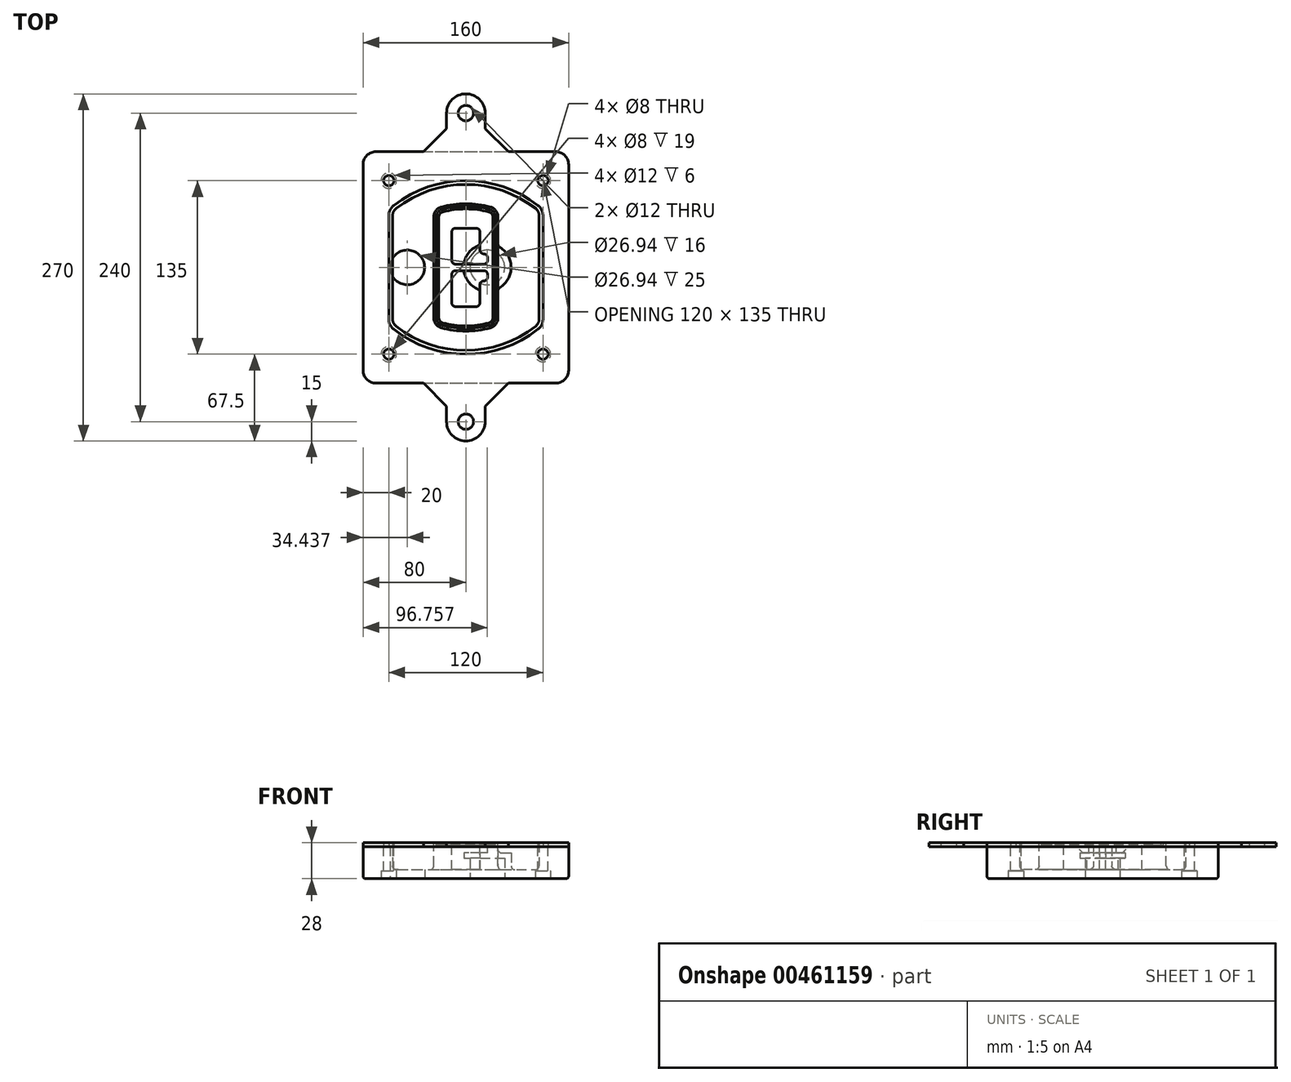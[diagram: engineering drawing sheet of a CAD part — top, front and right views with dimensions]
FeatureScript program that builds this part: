
annotation { "Feature Type Name" : "Feature", "Feature Type Description" : "" }
export const myFeature = defineFeature(function(context is Context, id is Id, definition is map)
    precondition{}
    {
        {
            var Q0;
            Q0=qCreatedBy(makeId("Top.planeOp"),FACE);
            var sketch = newSketch(context, id + "F0", { "sketchPlane" : qUnion([Q0])});
            skPoint(sketch, "E0.rect.middle", {"position": v(0, 0) * mm});
            skLineSegment(sketch, "E1.bottom", {"start": v(-70, -90) * mm, "end": v(70, -90) * mm});
            skLineSegment(sketch, "E1.top", {"start": v(-70, 90) * mm, "end": v(70, 90) * mm});
            skLineSegment(sketch, "E1.left", {"start": v(-80, -80) * mm, "end": v(-80, 80) * mm});
            skLineSegment(sketch, "E1.right", {"start": v(80, -80) * mm, "end": v(80, 80) * mm});
            skLineSegment(sketch, "E2", {"start": v(-80, 90) * mm, "end": v(80, -90) * mm, "construction": true});
            skLineSegment(sketch, "E3", {"start": v(80, 90) * mm, "end": v(-80, -90) * mm, "construction": true});
            skCircle(sketch, "E4", {"center": v(-60, 67.5) * mm, "radius": 4 * mm});
            skCircle(sketch, "E5", {"center": v(60, 67.5) * mm, "radius": 4 * mm});
            skCircle(sketch, "E6", {"center": v(60, -67.5) * mm, "radius": 4 * mm});
            skCircle(sketch, "E7", {"center": v(-60, -67.5) * mm, "radius": 4 * mm});
            skLineSegment(sketch, "E8", {"start": v(-60, 67.5) * mm, "end": v(60, 67.5) * mm, "construction": true});
            skLineSegment(sketch, "E9", {"start": v(60, 67.5) * mm, "end": v(60, -67.5) * mm, "construction": true});
            skLineSegment(sketch, "E10", {"start": v(60, -67.5) * mm, "end": v(-60, -67.5) * mm, "construction": true});
            skLineSegment(sketch, "E11", {"start": v(-60, -67.5) * mm, "end": v(-60, 67.5) * mm, "construction": true});
            skLineSegment(sketch, "E12", {"start": v(-60, 40.3) * mm, "end": v(-60, -40.3) * mm});
            skLineSegment(sketch, "E13", {"start": v(60, 40.3) * mm, "end": v(60, -40.3) * mm});
            skArc(sketch, "E14", {"start": v(56.15, 48.18) * mm, "mid": v(0, 67.5) * mm, "end": v(-56.15, 48.18) * mm});
            skArc(sketch, "E15", {"start": v(-56.15, -48.18) * mm, "mid": v(0, -67.5) * mm, "end": v(56.15, -48.18) * mm});
            skLineSegment(sketch, "E16", {"start": v(-60, 0) * mm, "end": v(60, 0) * mm, "construction": true});
            skPoint(sketch, "E17.visualSharp", {"position": v(-60, -45) * mm});
            skArc(sketch, "E17.filletArc", {"start": v(-60, -40.3) * mm, "mid": v(-58.99, -44.68) * mm, "end": v(-56.15, -48.18) * mm});
            skPoint(sketch, "E18.visualSharp", {"position": v(-60, 45) * mm});
            skArc(sketch, "E18.filletArc", {"start": v(-56.15, 48.18) * mm, "mid": v(-58.99, 44.68) * mm, "end": v(-60, 40.3) * mm});
            skPoint(sketch, "E19.visualSharp", {"position": v(60, 45) * mm});
            skArc(sketch, "E19.filletArc", {"start": v(60, 40.3) * mm, "mid": v(58.99, 44.68) * mm, "end": v(56.15, 48.18) * mm});
            skPoint(sketch, "E20.visualSharp", {"position": v(60, -45) * mm});
            skArc(sketch, "E20.filletArc", {"start": v(56.15, -48.18) * mm, "mid": v(58.99, -44.68) * mm, "end": v(60, -40.3) * mm});
            skPoint(sketch, "E21.visualSharp", {"position": v(-80, 90) * mm});
            skArc(sketch, "E21.filletArc", {"start": v(-70, 90) * mm, "mid": v(-77.07, 87.07) * mm, "end": v(-80, 80) * mm});
            skPoint(sketch, "E22.visualSharp", {"position": v(80, 90) * mm});
            skArc(sketch, "E22.filletArc", {"start": v(80, 80) * mm, "mid": v(77.07, 87.07) * mm, "end": v(70, 90) * mm});
            skPoint(sketch, "E23.visualSharp", {"position": v(80, -90) * mm});
            skArc(sketch, "E23.filletArc", {"start": v(70, -90) * mm, "mid": v(77.07, -87.07) * mm, "end": v(80, -80) * mm});
            skPoint(sketch, "E24.visualSharp", {"position": v(-80, -90) * mm});
            skArc(sketch, "E24.filletArc", {"start": v(-80, -80) * mm, "mid": v(-77.07, -87.07) * mm, "end": v(-70, -90) * mm});
            skArc(sketch, "E25.0", {"start": v(57, 40.3) * mm, "mid": v(56.3, 43.36) * mm, "end": v(54.3, 45.81) * mm});
            skLineSegment(sketch, "E25.1", {"start": v(57, 40.3) * mm, "end": v(57, -40.3) * mm});
            skArc(sketch, "E25.2", {"start": v(54.3, -45.81) * mm, "mid": v(56.3, -43.36) * mm, "end": v(57, -40.3) * mm});
            skArc(sketch, "E25.3", {"start": v(-54.3, -45.81) * mm, "mid": v(0, -64.5) * mm, "end": v(54.3, -45.81) * mm});
            skArc(sketch, "E25.4", {"start": v(-57, -40.3) * mm, "mid": v(-56.3, -43.36) * mm, "end": v(-54.3, -45.81) * mm});
            skArc(sketch, "E25.5", {"start": v(54.3, 45.81) * mm, "mid": v(0, 64.5) * mm, "end": v(-54.3, 45.81) * mm});
            skLineSegment(sketch, "E25.6", {"start": v(-57, 40.3) * mm, "end": v(-57, -40.3) * mm});
            skArc(sketch, "E25.7", {"start": v(-54.3, 45.81) * mm, "mid": v(-56.3, 43.36) * mm, "end": v(-57, 40.3) * mm});
            skArc(sketch, "E26.0", {"start": v(-58.62, 51.33) * mm, "mid": v(-62.58, 46.43) * mm, "end": v(-64, 40.3) * mm});
            skArc(sketch, "E26.1", {"start": v(58.62, 51.33) * mm, "mid": v(0, 71.5) * mm, "end": v(-58.62, 51.33) * mm});
            skArc(sketch, "E26.2", {"start": v(64, 40.3) * mm, "mid": v(62.58, 46.43) * mm, "end": v(58.62, 51.33) * mm});
            skLineSegment(sketch, "E26.3", {"start": v(64, 40.3) * mm, "end": v(64, -40.3) * mm});
            skArc(sketch, "E26.4", {"start": v(58.62, -51.33) * mm, "mid": v(62.58, -46.43) * mm, "end": v(64, -40.3) * mm});
            skLineSegment(sketch, "E26.5", {"start": v(-64, 40.3) * mm, "end": v(-64, -40.3) * mm});
            skArc(sketch, "E26.6", {"start": v(-58.62, -51.33) * mm, "mid": v(0, -71.5) * mm, "end": v(58.62, -51.33) * mm});
            skArc(sketch, "E26.7", {"start": v(-64, -40.3) * mm, "mid": v(-62.58, -46.43) * mm, "end": v(-58.62, -51.33) * mm});
            skSolve(sketch);
        }
        {
            var Q0;
            Q0=makeQuery(id+"F0.imprint","IMPRINT",FACE,{"disambiguationData":[TD([[makeQuery(id+"F0.imprint","IMPRINT",EDGE,{"derivedFrom":sQuery(id+"F0.wireOp",EDGE,"E1.bottom")}),1.0]])]});
            var Q1;
            Q1=makeQuery(id+"F0.imprint","IMPRINT",FACE,{"disambiguationData":[TD([[makeQuery(id+"F0.imprint","IMPRINT",EDGE,{"derivedFrom":sQuery(id+"F0.wireOp",EDGE,"E12")}),1.0]])]});
            var Q2;
            Q2=makeQuery(id+"F0.imprint","IMPRINT",FACE,{"disambiguationData":[TD([[makeQuery(id+"F0.imprint","IMPRINT",EDGE,{"derivedFrom":sQuery(id+"F0.wireOp",EDGE,"E25.0")}),1.0]])]});
            var Q3;
            Q3=makeQuery(id+"F0.imprint","IMPRINT",FACE,{"disambiguationData":[TD([[makeQuery(id+"F0.imprint","IMPRINT",EDGE,{"derivedFrom":sQuery(id+"F0.wireOp",EDGE,"E12")}),-1.0]])]});
            extrude(context, id + "F1", {"entities" : qUnion([Q0, Q1, Q2, Q3]), "oppositeDirection" : true, "depth" : 25 * mm});
        }
        {
            var Q0;
            Q0=makeQuery(id+"F0.imprint","IMPRINT",FACE,{"disambiguationData":[TD([[makeQuery(id+"F0.imprint","IMPRINT",EDGE,{"derivedFrom":sQuery(id+"F0.wireOp",EDGE,"E12")}),1.0]])]});
            extrude(context, id + "F2", {"entities" : qUnion([Q0]), "operationType" : NewBodyOperationType.ADD, "depth" : 3 * mm});
        }
        {
            var Q0;
            Q0=makeQuery(id+"F0.imprint","IMPRINT",FACE,{"disambiguationData":[TD([[makeQuery(id+"F0.imprint","IMPRINT",EDGE,{"derivedFrom":sQuery(id+"F0.wireOp",EDGE,"E25.0")}),1.0]])]});
            extrude(context, id + "F3", {"entities" : qUnion([Q0]), "operationType" : NewBodyOperationType.REMOVE, "oppositeDirection" : true, "depth" : 18 * mm});
        }
        {
            var Q0;
            Q0=makeQuery(id+"F2.opExtrude","CAP_FACE",FACE,{"disambiguationData":[OSD([sQuery(id+"F0.wireOp",EDGE,"E12"),sQuery(id+"F0.wireOp",EDGE,"E13"),sQuery(id+"F0.wireOp",EDGE,"E14"),sQuery(id+"F0.wireOp",EDGE,"E15"),sQuery(id+"F0.wireOp",EDGE,"E17.filletArc"),sQuery(id+"F0.wireOp",EDGE,"E18.filletArc"),sQuery(id+"F0.wireOp",EDGE,"E19.filletArc"),sQuery(id+"F0.wireOp",EDGE,"E20.filletArc"),sQuery(id+"F0.wireOp",EDGE,"E25.0"),sQuery(id+"F0.wireOp",EDGE,"E25.1"),sQuery(id+"F0.wireOp",EDGE,"E25.2"),sQuery(id+"F0.wireOp",EDGE,"E25.3"),sQuery(id+"F0.wireOp",EDGE,"E25.4"),sQuery(id+"F0.wireOp",EDGE,"E25.5"),sQuery(id+"F0.wireOp",EDGE,"E25.6"),sQuery(id+"F0.wireOp",EDGE,"E25.7")])],"isStart":false});
            var sketch = newSketch(context, id + "F4", { "sketchPlane" : qUnion([Q0])});
            skArc(sketch, "E27.0", {"start": v(-19.08, -46.97) * mm, "mid": v(0, -49.5) * mm, "end": v(19.08, -46.97) * mm});
            skArc(sketch, "E28.0", {"start": v(19.08, 46.97) * mm, "mid": v(0, 49.5) * mm, "end": v(-19.08, 46.97) * mm});
            skLineSegment(sketch, "E29", {"start": v(-25, 39.25) * mm, "end": v(-25, -39.25) * mm});
            skLineSegment(sketch, "E30", {"start": v(25, 39.25) * mm, "end": v(25, -39.25) * mm});
            skLineSegment(sketch, "E31", {"start": v(-25, 45.1) * mm, "end": v(25, 45.1) * mm, "construction": true});
            skLineSegment(sketch, "E32", {"start": v(-25, -45.1) * mm, "end": v(25, -45.1) * mm, "construction": true});
            skPoint(sketch, "E33.visualSharp", {"position": v(-25, 45.1) * mm});
            skArc(sketch, "E33.filletArc", {"start": v(-19.08, 46.97) * mm, "mid": v(-23.35, 44.11) * mm, "end": v(-25, 39.25) * mm});
            skPoint(sketch, "E34.visualSharp", {"position": v(25, 45.1) * mm});
            skArc(sketch, "E34.filletArc", {"start": v(25, 39.25) * mm, "mid": v(23.35, 44.11) * mm, "end": v(19.08, 46.97) * mm});
            skPoint(sketch, "E35.visualSharp", {"position": v(25, -45.1) * mm});
            skArc(sketch, "E35.filletArc", {"start": v(19.08, -46.97) * mm, "mid": v(23.35, -44.11) * mm, "end": v(25, -39.25) * mm});
            skPoint(sketch, "E36.visualSharp", {"position": v(-25, -45.1) * mm});
            skArc(sketch, "E36.filletArc", {"start": v(-25, -39.25) * mm, "mid": v(-23.35, -44.11) * mm, "end": v(-19.08, -46.97) * mm});
            skArc(sketch, "E37.0", {"start": v(54.3, 45.81) * mm, "mid": v(0, 64.5) * mm, "end": v(-54.3, 45.81) * mm});
            skArc(sketch, "E37.1", {"start": v(-54.3, 45.81) * mm, "mid": v(-56.3, 43.36) * mm, "end": v(-57, 40.3) * mm});
            skLineSegment(sketch, "E37.2", {"start": v(-57, 40.3) * mm, "end": v(-57, -40.3) * mm});
            skArc(sketch, "E37.3", {"start": v(-57, -40.3) * mm, "mid": v(-56.3, -43.36) * mm, "end": v(-54.3, -45.81) * mm});
            skArc(sketch, "E37.4", {"start": v(-54.3, -45.81) * mm, "mid": v(0, -64.5) * mm, "end": v(54.3, -45.81) * mm});
            skArc(sketch, "E37.5", {"start": v(54.3, -45.81) * mm, "mid": v(56.3, -43.36) * mm, "end": v(57, -40.3) * mm});
            skLineSegment(sketch, "E37.6", {"start": v(57, 40.3) * mm, "end": v(57, -40.3) * mm});
            skArc(sketch, "E37.7", {"start": v(57, 40.3) * mm, "mid": v(56.3, 43.36) * mm, "end": v(54.3, 45.81) * mm});
            skLineSegment(sketch, "E38.0", {"start": v(23, 39.25) * mm, "end": v(23, -39.25) * mm});
            skArc(sketch, "E38.1", {"start": v(18.56, -45.04) * mm, "mid": v(21.76, -42.9) * mm, "end": v(23, -39.25) * mm});
            skArc(sketch, "E38.2", {"start": v(-18.56, -45.04) * mm, "mid": v(0, -47.5) * mm, "end": v(18.56, -45.04) * mm});
            skArc(sketch, "E38.3", {"start": v(-23, -39.25) * mm, "mid": v(-21.76, -42.9) * mm, "end": v(-18.56, -45.04) * mm});
            skLineSegment(sketch, "E38.4", {"start": v(-23, 39.25) * mm, "end": v(-23, -39.25) * mm});
            skArc(sketch, "E38.5", {"start": v(23, 39.25) * mm, "mid": v(21.76, 42.9) * mm, "end": v(18.56, 45.04) * mm});
            skArc(sketch, "E38.6", {"start": v(-18.56, 45.04) * mm, "mid": v(-21.76, 42.9) * mm, "end": v(-23, 39.25) * mm});
            skArc(sketch, "E38.7", {"start": v(18.56, 45.04) * mm, "mid": v(0, 47.5) * mm, "end": v(-18.56, 45.04) * mm});
            skArc(sketch, "E39.0", {"start": v(21, 39.25) * mm, "mid": v(20.18, 41.68) * mm, "end": v(18.04, 43.1) * mm});
            skLineSegment(sketch, "E39.1", {"start": v(21, 39.25) * mm, "end": v(21, -39.25) * mm});
            skArc(sketch, "E39.2", {"start": v(18.04, -43.1) * mm, "mid": v(20.18, -41.68) * mm, "end": v(21, -39.25) * mm});
            skArc(sketch, "E39.3", {"start": v(-18.04, -43.1) * mm, "mid": v(0, -45.5) * mm, "end": v(18.04, -43.1) * mm});
            skArc(sketch, "E39.4", {"start": v(-21, -39.25) * mm, "mid": v(-20.18, -41.68) * mm, "end": v(-18.04, -43.1) * mm});
            skArc(sketch, "E39.5", {"start": v(18.04, 43.1) * mm, "mid": v(0, 45.5) * mm, "end": v(-18.04, 43.1) * mm});
            skLineSegment(sketch, "E39.6", {"start": v(-21, 39.25) * mm, "end": v(-21, -39.25) * mm});
            skArc(sketch, "E39.7", {"start": v(-18.04, 43.1) * mm, "mid": v(-20.18, 41.68) * mm, "end": v(-21, 39.25) * mm});
            skLineSegment(sketch, "E40", {"start": v(-25, 0) * mm, "end": v(25, 0) * mm, "construction": true});
            skLineSegment(sketch, "E41", {"start": v(-11, 5.5) * mm, "end": v(-11, 27.5) * mm});
            skLineSegment(sketch, "E42", {"start": v(-8, 30.5) * mm, "end": v(8, 30.5) * mm});
            skLineSegment(sketch, "E43", {"start": v(11, 27.5) * mm, "end": v(11, 13.5) * mm});
            skLineSegment(sketch, "E44", {"start": v(14, 10.5) * mm, "end": v(14, 10.5) * mm});
            skLineSegment(sketch, "E45", {"start": v(17, 7.5) * mm, "end": v(17, 5.5) * mm});
            skLineSegment(sketch, "E46", {"start": v(14, 2.5) * mm, "end": v(-8, 2.5) * mm});
            skPoint(sketch, "E47.visualSharp", {"position": v(-11, 30.5) * mm});
            skArc(sketch, "E47.filletArc", {"start": v(-8, 30.5) * mm, "mid": v(-10.12, 29.62) * mm, "end": v(-11, 27.5) * mm});
            skPoint(sketch, "E48.visualSharp", {"position": v(11, 30.5) * mm});
            skArc(sketch, "E48.filletArc", {"start": v(11, 27.5) * mm, "mid": v(10.12, 29.62) * mm, "end": v(8, 30.5) * mm});
            skPoint(sketch, "E49.visualSharp", {"position": v(11, 10.5) * mm});
            skArc(sketch, "E49.filletArc", {"start": v(11, 13.5) * mm, "mid": v(11.88, 11.38) * mm, "end": v(14, 10.5) * mm});
            skPoint(sketch, "E50.visualSharp", {"position": v(17, 10.5) * mm});
            skArc(sketch, "E50.filletArc", {"start": v(17, 7.5) * mm, "mid": v(16.12, 9.62) * mm, "end": v(14, 10.5) * mm});
            skPoint(sketch, "E51.visualSharp", {"position": v(17, 2.5) * mm});
            skArc(sketch, "E51.filletArc", {"start": v(14, 2.5) * mm, "mid": v(16.12, 3.38) * mm, "end": v(17, 5.5) * mm});
            skPoint(sketch, "E52.visualSharp", {"position": v(-11, 2.5) * mm});
            skArc(sketch, "E52.filletArc", {"start": v(-11, 5.5) * mm, "mid": v(-10.12, 3.38) * mm, "end": v(-8, 2.5) * mm});
            skLineSegment(sketch, "E53.0.MirrorCS", {"start": v(14, -2.5) * mm, "end": v(-8, -2.5) * mm});
            skArc(sketch, "E54.0.MirrorCS", {"start": v(-11, -5.5) * mm, "mid": v(-10.12, -3.38) * mm, "end": v(-8, -2.5) * mm});
            skLineSegment(sketch, "E55.0.MirrorCS", {"start": v(-11, -5.5) * mm, "end": v(-11, -27.5) * mm});
            skArc(sketch, "E56.0.MirrorCS", {"start": v(-8, -30.5) * mm, "mid": v(-10.12, -29.62) * mm, "end": v(-11, -27.5) * mm});
            skLineSegment(sketch, "E57.0.MirrorCS", {"start": v(-8, -30.5) * mm, "end": v(8, -30.5) * mm});
            skArc(sketch, "E58.0.MirrorCS", {"start": v(11, -27.5) * mm, "mid": v(10.12, -29.62) * mm, "end": v(8, -30.5) * mm});
            skLineSegment(sketch, "E59.0.MirrorCS", {"start": v(11, -27.5) * mm, "end": v(11, -13.5) * mm});
            skArc(sketch, "E60.0.MirrorCS", {"start": v(11, -13.5) * mm, "mid": v(11.88, -11.38) * mm, "end": v(14, -10.5) * mm});
            skArc(sketch, "E61.0.MirrorCS", {"start": v(17, -7.5) * mm, "mid": v(16.12, -9.62) * mm, "end": v(14, -10.5) * mm});
            skLineSegment(sketch, "E62.0.MirrorCS", {"start": v(17, -7.5) * mm, "end": v(17, -5.5) * mm});
            skArc(sketch, "E63.0.MirrorCS", {"start": v(14, -2.5) * mm, "mid": v(16.12, -3.38) * mm, "end": v(17, -5.5) * mm});
            skSolve(sketch);
        }
        {
            var Q0;
            Q0=makeQuery(id+"F4.imprint","IMPRINT",FACE,{"disambiguationData":[TD([[makeQuery(id+"F4.imprint","IMPRINT",EDGE,{"derivedFrom":sQuery(id+"F4.wireOp",EDGE,"E27.0")}),1.0]])]});
            var Q1;
            Q1=makeQuery(id+"F4.imprint","IMPRINT",FACE,{"disambiguationData":[TD([[makeQuery(id+"F4.imprint","IMPRINT",EDGE,{"derivedFrom":sQuery(id+"F4.wireOp",EDGE,"E38.0")}),-1.0]])]});
            var Q2;
            Q2=makeQuery(id+"F4.imprint","IMPRINT",FACE,{"disambiguationData":[TD([[makeQuery(id+"F4.imprint","IMPRINT",EDGE,{"derivedFrom":sQuery(id+"F4.wireOp",EDGE,"E39.0")}),1.0]])]});
            extrude(context, id + "F5", {"entities" : qUnion([Q0, Q1, Q2]), "operationType" : NewBodyOperationType.ADD, "endBound" : BoundingType.UP_TO_NEXT, "oppositeDirection" : true, "depth" : 25 * mm});
        }
        {
            var Q0;
            Q0=makeQuery(id+"F4.imprint","IMPRINT",FACE,{"disambiguationData":[TD([[makeQuery(id+"F4.imprint","IMPRINT",EDGE,{"derivedFrom":sQuery(id+"F4.wireOp",EDGE,"E38.0")}),-1.0]])]});
            extrude(context, id + "F6", {"entities" : qUnion([Q0]), "operationType" : NewBodyOperationType.REMOVE, "oppositeDirection" : true, "depth" : 2 * mm});
        }
        {
            var Q0;
            Q0=makeQuery(id+"F1.opExtrude","CAP_FACE",FACE,{"disambiguationData":[OSD([sQuery(id+"F0.wireOp",EDGE,"E1.bottom"),sQuery(id+"F0.wireOp",EDGE,"E1.top"),sQuery(id+"F0.wireOp",EDGE,"E1.left"),sQuery(id+"F0.wireOp",EDGE,"E1.right"),sQuery(id+"F0.wireOp",EDGE,"E4"),sQuery(id+"F0.wireOp",EDGE,"E5"),sQuery(id+"F0.wireOp",EDGE,"E6"),sQuery(id+"F0.wireOp",EDGE,"E7"),sQuery(id+"F0.wireOp",EDGE,"E21.filletArc"),sQuery(id+"F0.wireOp",EDGE,"E22.filletArc"),sQuery(id+"F0.wireOp",EDGE,"E23.filletArc"),sQuery(id+"F0.wireOp",EDGE,"E24.filletArc")])],"isStart":false});
            var sketch = newSketch(context, id + "F7", { "sketchPlane" : qUnion([Q0])});
            skCircle(sketch, "E64", {"center": v(16.76, 0) * mm, "radius": 13.47 * mm});
            skCircle(sketch, "E65", {"center": v(-45.56, 0) * mm, "radius": 13.47 * mm});
            skLineSegment(sketch, "E66", {"start": v(80, 0) * mm, "end": v(-80, 0) * mm});
            skCircle(sketch, "E67", {"center": v(16.76, 0) * mm, "radius": 18.47 * mm});
            skCircle(sketch, "E68", {"center": v(60, -67.5) * mm, "radius": 6 * mm});
            skCircle(sketch, "E69", {"center": v(-60, -67.5) * mm, "radius": 6 * mm});
            skCircle(sketch, "E70", {"center": v(-60, 67.5) * mm, "radius": 6 * mm});
            skCircle(sketch, "E71", {"center": v(60, 67.5) * mm, "radius": 6 * mm});
            skSolve(sketch);
        }
        {
            var Q0;
            {var subQ1=sQuery(id+"F7.wireOp",EDGE,"E66");var subQ4=sQuery(id+"F7.wireOp",EDGE,"E64");var subQ6=makeQuery(id+"F7.imprint","INTERSECT",VERTEX,{"disambiguationData":[OD(0.0)],"derivedFrom":[subQ4,subQ1]});Q0=makeQuery(id+"F7.imprint","IMPRINT",FACE,{"disambiguationData":[TD([[makeQuery(id+"F7.imprint","IMPRINT",EDGE,{"disambiguationData":[TD([[subQ6,-1.0]])],"derivedFrom":subQ4}),-1.0]])]});}
            var Q1;
            {var subQ0=sQuery(id+"F7.wireOp",EDGE,"E66");var subQ1=sQuery(id+"F7.wireOp",EDGE,"E64");var subQ3=makeQuery(id+"F7.imprint","INTERSECT",VERTEX,{"disambiguationData":[OD(0.0)],"derivedFrom":[subQ1,subQ0]});Q1=makeQuery(id+"F7.imprint","IMPRINT",FACE,{"disambiguationData":[TD([[makeQuery(id+"F7.imprint","IMPRINT",EDGE,{"disambiguationData":[TD([[subQ3,-1.0]])],"derivedFrom":subQ1}),1.0]])]});}
            var Q2;
            {var subQ0=sQuery(id+"F7.wireOp",EDGE,"E66");var subQ1=sQuery(id+"F7.wireOp",EDGE,"E64");var subQ3=makeQuery(id+"F7.imprint","INTERSECT",VERTEX,{"disambiguationData":[OD(0.0)],"derivedFrom":[subQ1,subQ0]});Q2=makeQuery(id+"F7.imprint","IMPRINT",FACE,{"disambiguationData":[TD([[makeQuery(id+"F7.imprint","IMPRINT",EDGE,{"disambiguationData":[TD([[subQ3,1.0]])],"derivedFrom":subQ1}),1.0]])]});}
            var Q3;
            {var subQ1=sQuery(id+"F7.wireOp",EDGE,"E66");var subQ4=sQuery(id+"F7.wireOp",EDGE,"E64");var subQ6=makeQuery(id+"F7.imprint","INTERSECT",VERTEX,{"disambiguationData":[OD(0.0)],"derivedFrom":[subQ4,subQ1]});Q3=makeQuery(id+"F7.imprint","IMPRINT",FACE,{"disambiguationData":[TD([[makeQuery(id+"F7.imprint","IMPRINT",EDGE,{"disambiguationData":[TD([[subQ6,1.0]])],"derivedFrom":subQ4}),-1.0]])]});}
            extrude(context, id + "F8", {"entities" : qUnion([Q0, Q1, Q2, Q3]), "operationType" : NewBodyOperationType.ADD, "oppositeDirection" : true, "depth" : 20 * mm});
        }
        {
            var Q0;
            {var subQ0=sQuery(id+"F7.wireOp",EDGE,"E66");var subQ1=sQuery(id+"F7.wireOp",EDGE,"E64");var subQ3=makeQuery(id+"F7.imprint","INTERSECT",VERTEX,{"disambiguationData":[OD(0.0)],"derivedFrom":[subQ1,subQ0]});Q0=makeQuery(id+"F7.imprint","IMPRINT",FACE,{"disambiguationData":[TD([[makeQuery(id+"F7.imprint","IMPRINT",EDGE,{"disambiguationData":[TD([[subQ3,-1.0]])],"derivedFrom":subQ1}),1.0]])]});}
            var Q1;
            {var subQ0=sQuery(id+"F7.wireOp",EDGE,"E66");var subQ1=sQuery(id+"F7.wireOp",EDGE,"E64");var subQ3=makeQuery(id+"F7.imprint","INTERSECT",VERTEX,{"disambiguationData":[OD(0.0)],"derivedFrom":[subQ1,subQ0]});Q1=makeQuery(id+"F7.imprint","IMPRINT",FACE,{"disambiguationData":[TD([[makeQuery(id+"F7.imprint","IMPRINT",EDGE,{"disambiguationData":[TD([[subQ3,1.0]])],"derivedFrom":subQ1}),1.0]])]});}
            extrude(context, id + "F9", {"entities" : qUnion([Q0, Q1]), "operationType" : NewBodyOperationType.REMOVE, "oppositeDirection" : true, "depth" : 16 * mm});
        }
        {
            var Q0;
            {var subQ0=sQuery(id+"F7.wireOp",EDGE,"E66");var subQ1=sQuery(id+"F7.wireOp",EDGE,"E65");var subQ3=makeQuery(id+"F7.imprint","INTERSECT",VERTEX,{"disambiguationData":[OD(0.0)],"derivedFrom":[subQ1,subQ0]});Q0=makeQuery(id+"F7.imprint","IMPRINT",FACE,{"disambiguationData":[TD([[makeQuery(id+"F7.imprint","IMPRINT",EDGE,{"disambiguationData":[TD([[subQ3,-1.0]])],"derivedFrom":subQ1}),1.0]])]});}
            var Q1;
            {var subQ0=sQuery(id+"F7.wireOp",EDGE,"E66");var subQ1=sQuery(id+"F7.wireOp",EDGE,"E65");var subQ3=makeQuery(id+"F7.imprint","INTERSECT",VERTEX,{"disambiguationData":[OD(0.0)],"derivedFrom":[subQ1,subQ0]});Q1=makeQuery(id+"F7.imprint","IMPRINT",FACE,{"disambiguationData":[TD([[makeQuery(id+"F7.imprint","IMPRINT",EDGE,{"disambiguationData":[TD([[subQ3,1.0]])],"derivedFrom":subQ1}),1.0]])]});}
            extrude(context, id + "F10", {"entities" : qUnion([Q0, Q1]), "operationType" : NewBodyOperationType.REMOVE, "oppositeDirection" : true, "depth" : 25 * mm});
        }
        {
            var Q0;
            Q0=makeQuery(id+"F7.imprint","IMPRINT",FACE,{"disambiguationData":[TD([[makeQuery(id+"F7.imprint","IMPRINT",EDGE,{"derivedFrom":sQuery(id+"F7.wireOp",EDGE,"E68")}),1.0]])]});
            var Q1;
            Q1=makeQuery(id+"F7.imprint","IMPRINT",FACE,{"disambiguationData":[TD([[makeQuery(id+"F7.imprint","IMPRINT",EDGE,{"derivedFrom":makeQuery(id+"F1.opExtrude","CAP_EDGE",EDGE,{"disambiguationData":[OSD([sQuery(id+"F0.wireOp",EDGE,"E5")])],"isStart":false})}),-1.0]])]});
            var Q2;
            Q2=makeQuery(id+"F7.imprint","IMPRINT",FACE,{"disambiguationData":[TD([[makeQuery(id+"F7.imprint","IMPRINT",EDGE,{"derivedFrom":sQuery(id+"F7.wireOp",EDGE,"E69")}),1.0]])]});
            var Q3;
            Q3=makeQuery(id+"F7.imprint","IMPRINT",FACE,{"disambiguationData":[TD([[makeQuery(id+"F7.imprint","IMPRINT",EDGE,{"derivedFrom":makeQuery(id+"F1.opExtrude","CAP_EDGE",EDGE,{"disambiguationData":[OSD([sQuery(id+"F0.wireOp",EDGE,"E4")])],"isStart":false})}),-1.0]])]});
            var Q4;
            Q4=makeQuery(id+"F7.imprint","IMPRINT",FACE,{"disambiguationData":[TD([[makeQuery(id+"F7.imprint","IMPRINT",EDGE,{"derivedFrom":sQuery(id+"F7.wireOp",EDGE,"E70")}),1.0]])]});
            var Q5;
            Q5=makeQuery(id+"F7.imprint","IMPRINT",FACE,{"disambiguationData":[TD([[makeQuery(id+"F7.imprint","IMPRINT",EDGE,{"derivedFrom":makeQuery(id+"F1.opExtrude","CAP_EDGE",EDGE,{"disambiguationData":[OSD([sQuery(id+"F0.wireOp",EDGE,"E7")])],"isStart":false})}),-1.0]])]});
            var Q6;
            Q6=makeQuery(id+"F7.imprint","IMPRINT",FACE,{"disambiguationData":[TD([[makeQuery(id+"F7.imprint","IMPRINT",EDGE,{"derivedFrom":sQuery(id+"F7.wireOp",EDGE,"E71")}),1.0]])]});
            var Q7;
            Q7=makeQuery(id+"F7.imprint","IMPRINT",FACE,{"disambiguationData":[TD([[makeQuery(id+"F7.imprint","IMPRINT",EDGE,{"derivedFrom":makeQuery(id+"F1.opExtrude","CAP_EDGE",EDGE,{"disambiguationData":[OSD([sQuery(id+"F0.wireOp",EDGE,"E6")])],"isStart":false})}),-1.0]])]});
            extrude(context, id + "F11", {"entities" : qUnion([Q0, Q1, Q2, Q3, Q4, Q5, Q6, Q7]), "operationType" : NewBodyOperationType.REMOVE, "oppositeDirection" : true, "depth" : 6 * mm});
        }
        {
            var Q0;
            Q0=makeQuery(id+"F9.boolean.opBoolean","COPY",FACE,{"derivedFrom":makeQuery(id+"F9.opExtrude","CAP_FACE",FACE,{"disambiguationData":[OSD([sQuery(id+"F7.wireOp",EDGE,"E64")])],"isStart":false})});
            var sketch = newSketch(context, id + "F12", { "sketchPlane" : qUnion([Q0])});
            skArc(sketch, "E72.0", {"start": v(11, 17.55) * mm, "mid": v(2.57, 11.82) * mm, "end": v(-1.54, 2.5) * mm});
            skArc(sketch, "E72.1", {"start": v(-1.54, -2.5) * mm, "mid": v(2.57, -11.82) * mm, "end": v(11, -17.55) * mm});
            skLineSegment(sketch, "E73", {"start": v(-1.54, -2.5) * mm, "end": v(14, -2.5) * mm});
            skLineSegment(sketch, "E74.0", {"start": v(14, 2.5) * mm, "end": v(-1.54, 2.5) * mm});
            skArc(sketch, "E74.1", {"start": v(14, 2.5) * mm, "mid": v(16.12, 3.38) * mm, "end": v(17, 5.5) * mm});
            skLineSegment(sketch, "E74.2", {"start": v(17, 7.5) * mm, "end": v(17, 5.5) * mm});
            skArc(sketch, "E74.3", {"start": v(17, 7.5) * mm, "mid": v(16.12, 9.62) * mm, "end": v(14, 10.5) * mm});
            skArc(sketch, "E74.4", {"start": v(11, 13.5) * mm, "mid": v(11.88, 11.38) * mm, "end": v(14, 10.5) * mm});
            skLineSegment(sketch, "E74.5", {"start": v(11, 17.55) * mm, "end": v(11, 13.5) * mm});
            skLineSegment(sketch, "E74.7", {"start": v(14, -2.5) * mm, "end": v(-1.54, -2.5) * mm});
            skArc(sketch, "E74.8", {"start": v(14, -2.5) * mm, "mid": v(16.12, -3.38) * mm, "end": v(17, -5.5) * mm});
            skLineSegment(sketch, "E74.9", {"start": v(17, -7.5) * mm, "end": v(17, -5.5) * mm});
            skArc(sketch, "E74.10", {"start": v(17, -7.5) * mm, "mid": v(16.12, -9.62) * mm, "end": v(14, -10.5) * mm});
            skArc(sketch, "E74.11", {"start": v(11, -13.5) * mm, "mid": v(11.88, -11.38) * mm, "end": v(14, -10.5) * mm});
            skLineSegment(sketch, "E74.12", {"start": v(11, -17.55) * mm, "end": v(11, -13.5) * mm});
            skPoint(sketch, "E75.orphan", {"position": v(11, -27.5) * mm});
            skPoint(sketch, "E76.orphan", {"position": v(-8, -2.5) * mm});
            skPoint(sketch, "E77.orphan", {"position": v(-8, 2.5) * mm});
            skPoint(sketch, "E78.orphan", {"position": v(11, 27.5) * mm});
            skSolve(sketch);
        }
        {
            var Q0;
            {var subQ7=sQuery(id+"F12.wireOp",EDGE,"E72.0");var subQ14=sQuery(id+"F12.wireOp",EDGE,"E72.1");var subQ16=sQuery(id+"F12.wireOp",EDGE,"E74.1");var subQ18=sQuery(id+"F12.wireOp",EDGE,"E74.8");Q0=qUnion([makeQuery(id+"F12.imprint","IMPRINT",FACE,{"disambiguationData":[TD([[makeQuery(id+"F12.imprint","IMPRINT",EDGE,{"derivedFrom":subQ7}),1.0]])]}),makeQuery(id+"F12.imprint","IMPRINT",FACE,{"disambiguationData":[TD([[makeQuery(id+"F12.imprint","IMPRINT",EDGE,{"derivedFrom":subQ14}),1.0]])]}),makeQuery(id+"F12.imprint","IMPRINT",FACE,{"disambiguationData":[TD([[makeQuery(id+"F12.imprint","IMPRINT",EDGE,{"derivedFrom":subQ16}),1.0]])]}),makeQuery(id+"F12.imprint","IMPRINT",FACE,{"disambiguationData":[TD([[makeQuery(id+"F12.imprint","IMPRINT",EDGE,{"derivedFrom":subQ18}),-1.0]])]})]);}
            var Q1;
            Q1=makeQuery(id+"F5.boolean.opBoolean","SPLIT",FACE,{"disambiguationData":[TD([makeQuery(id+"F5.opExtrude","SWEPT_FACE",FACE,{"disambiguationData":[OSD([sQuery(id+"F4.wireOp",EDGE,"E41")])]})])],"derivedFrom":makeQuery(id+"F3.boolean.opBoolean","COPY",FACE,{"derivedFrom":makeQuery(id+"F3.opExtrude","CAP_FACE",FACE,{"disambiguationData":[OSD([sQuery(id+"F0.wireOp",EDGE,"E25.0"),sQuery(id+"F0.wireOp",EDGE,"E25.1"),sQuery(id+"F0.wireOp",EDGE,"E25.2"),sQuery(id+"F0.wireOp",EDGE,"E25.3"),sQuery(id+"F0.wireOp",EDGE,"E25.4"),sQuery(id+"F0.wireOp",EDGE,"E25.5"),sQuery(id+"F0.wireOp",EDGE,"E25.6"),sQuery(id+"F0.wireOp",EDGE,"E25.7")])],"isStart":false})})});
            extrude(context, id + "F13", {"entities" : qUnion([Q0]), "operationType" : NewBodyOperationType.REMOVE, "endBound" : BoundingType.UP_TO_SURFACE, "endBoundEntityFace" : qUnion([Q1]), "depth" : 25 * mm});
        }
        {
            var Q0;
            Q0=makeQuery(id+"F3.boolean.opBoolean","COPY",EDGE,{"derivedFrom":makeQuery(id+"F3.opExtrude","CAP_EDGE",EDGE,{"disambiguationData":[OSD([sQuery(id+"F0.wireOp",EDGE,"E25.6")])],"isStart":false})});
            var Q1;
            Q1=makeQuery(id+"F8.boolean.opBoolean","INTERSECT",EDGE,{"derivedFrom":[makeQuery(id+"F5.opExtrude","SWEPT_FACE",FACE,{"disambiguationData":[OSD([sQuery(id+"F4.wireOp",EDGE,"E30")])]}),makeQuery(id+"F8.opExtrude","CAP_FACE",FACE,{"disambiguationData":[OSD([sQuery(id+"F7.wireOp",EDGE,"E67")])],"isStart":false})]});
            var Q2;
            Q2=makeQuery(id+"F8.boolean.opBoolean","INTERSECT",EDGE,{"disambiguationData":[OD(1.0)],"derivedFrom":[makeQuery(id+"F5.opExtrude","SWEPT_FACE",FACE,{"disambiguationData":[OSD([sQuery(id+"F4.wireOp",EDGE,"E30")])]}),makeQuery(id+"F8.opExtrude","SWEPT_FACE",FACE,{"disambiguationData":[OSD([sQuery(id+"F7.wireOp",EDGE,"E67")])]})]});
            var Q3;
            {var subQ0=sQuery(id+"F4.wireOp",EDGE,"E30");Q3=makeQuery(id+"F8.boolean.opBoolean","SPLIT",EDGE,{"disambiguationData":[TD([makeQuery(id+"F5.opExtrude","SWEPT_FACE",FACE,{"disambiguationData":[OSD([sQuery(id+"F4.wireOp",EDGE,"E35.filletArc")])]})])],"derivedFrom":makeQuery(id+"F5.opExtrude","CAP_EDGE",EDGE,{"disambiguationData":[OSD([subQ0])],"isStart":false})});}
            var Q4;
            {var subQ0=sQuery(id+"F0.wireOp",EDGE,"E25.7");var subQ1=sQuery(id+"F0.wireOp",EDGE,"E25.1");var subQ2=sQuery(id+"F0.wireOp",EDGE,"E25.6");var subQ3=sQuery(id+"F0.wireOp",EDGE,"E25.5");var subQ4=sQuery(id+"F0.wireOp",EDGE,"E25.4");var subQ5=sQuery(id+"F0.wireOp",EDGE,"E25.0");var subQ6=sQuery(id+"F0.wireOp",EDGE,"E25.2");var subQ7=sQuery(id+"F0.wireOp",EDGE,"E25.3");Q4=makeQuery(id+"F8.boolean.opBoolean","INTERSECT",EDGE,{"derivedFrom":[makeQuery(id+"F5.boolean.opBoolean","SPLIT",FACE,{"disambiguationData":[TD([makeQuery(id+"F2.opExtrude","SWEPT_FACE",FACE,{"disambiguationData":[OSD([subQ5])]})])],"derivedFrom":makeQuery(id+"F3.boolean.opBoolean","COPY",FACE,{"derivedFrom":makeQuery(id+"F3.opExtrude","CAP_FACE",FACE,{"disambiguationData":[OSD([subQ5,subQ1,subQ6,subQ7,subQ4,subQ3,subQ2,subQ0])],"isStart":false})})}),makeQuery(id+"F8.opExtrude","SWEPT_FACE",FACE,{"disambiguationData":[OSD([sQuery(id+"F7.wireOp",EDGE,"E67")])]})]});}
            var Q5;
            Q5=makeQuery(id+"F8.boolean.opBoolean","INTERSECT",EDGE,{"disambiguationData":[OD(0.0)],"derivedFrom":[makeQuery(id+"F5.opExtrude","SWEPT_FACE",FACE,{"disambiguationData":[OSD([sQuery(id+"F4.wireOp",EDGE,"E30")])]}),makeQuery(id+"F8.opExtrude","SWEPT_FACE",FACE,{"disambiguationData":[OSD([sQuery(id+"F7.wireOp",EDGE,"E67")])]})]});
            fillet(context, id + "F14", {"entities" : qUnion([Q0, Q1, Q2, Q3, Q4, Q5]), "radius" : 3 * mm, "tangentPropagation" : true, "allowEdgeOverflow" : false});
        }
        {
            var Q0;
            Q0=makeQuery(id+"F1.opExtrude","CAP_EDGE",EDGE,{"disambiguationData":[OSD([sQuery(id+"F0.wireOp",EDGE,"E1.bottom")])],"isStart":false});
            fillet(context, id + "F15", {"entities" : qUnion([Q0]), "radius" : 2 * mm, "tangentPropagation" : true, "allowEdgeOverflow" : false});
        }
        {
            var Q0;
            {var subQ0=sQuery(id+"F0.wireOp",EDGE,"E21.filletArc");var subQ1=sQuery(id+"F0.wireOp",EDGE,"E7");var subQ2=sQuery(id+"F0.wireOp",EDGE,"E6");var subQ3=sQuery(id+"F0.wireOp",EDGE,"E5");var subQ4=sQuery(id+"F0.wireOp",EDGE,"E4");var subQ5=sQuery(id+"F0.wireOp",EDGE,"E22.filletArc");var subQ6=sQuery(id+"F0.wireOp",EDGE,"E1.bottom");var subQ7=sQuery(id+"F0.wireOp",EDGE,"E1.right");var subQ8=sQuery(id+"F0.wireOp",EDGE,"E1.top");var subQ9=sQuery(id+"F0.wireOp",EDGE,"E1.left");var subQ10=sQuery(id+"F0.wireOp",EDGE,"E23.filletArc");var subQ11=sQuery(id+"F0.wireOp",EDGE,"E24.filletArc");Q0=makeQuery(id+"F2.boolean.opBoolean","SPLIT",FACE,{"disambiguationData":[TD([makeQuery(id+"F1.opExtrude","SWEPT_FACE",FACE,{"disambiguationData":[OSD([subQ6])]})])],"derivedFrom":makeQuery(id+"F1.opExtrude","CAP_FACE",FACE,{"disambiguationData":[OSD([subQ6,subQ8,subQ9,subQ7,subQ4,subQ3,subQ2,subQ1,subQ0,subQ5,subQ10,subQ11])],"isStart":true})});}
            var sketch = newSketch(context, id + "F16", { "sketchPlane" : qUnion([Q0])});
            skLineSegment(sketch, "E79.0", {"start": v(-70, 90) * mm, "end": v(70, 90) * mm});
            skArc(sketch, "E79.1", {"start": v(-70, 90) * mm, "mid": v(-77.07, 87.07) * mm, "end": v(-80, 80) * mm});
            skLineSegment(sketch, "E79.2", {"start": v(-80, -80) * mm, "end": v(-80, 80) * mm});
            skArc(sketch, "E79.3", {"start": v(-80, -80) * mm, "mid": v(-77.07, -87.07) * mm, "end": v(-70, -90) * mm});
            skLineSegment(sketch, "E79.4", {"start": v(-70, -90) * mm, "end": v(70, -90) * mm});
            skArc(sketch, "E79.5", {"start": v(70, -90) * mm, "mid": v(77.07, -87.07) * mm, "end": v(80, -80) * mm});
            skLineSegment(sketch, "E79.6", {"start": v(80, -80) * mm, "end": v(80, 80) * mm});
            skArc(sketch, "E79.7", {"start": v(80, 80) * mm, "mid": v(77.07, 87.07) * mm, "end": v(70, 90) * mm});
            skCircle(sketch, "E79.8", {"center": v(60, 67.5) * mm, "radius": 4 * mm});
            skCircle(sketch, "E79.9", {"center": v(-60, 67.5) * mm, "radius": 4 * mm});
            skCircle(sketch, "E79.10", {"center": v(-60, -67.5) * mm, "radius": 4 * mm});
            skCircle(sketch, "E79.11", {"center": v(60, -67.5) * mm, "radius": 4 * mm});
            skArc(sketch, "E79.12", {"start": v(-56.15, 48.18) * mm, "mid": v(-58.99, 44.68) * mm, "end": v(-60, 40.3) * mm});
            skArc(sketch, "E79.13", {"start": v(56.15, 48.18) * mm, "mid": v(0, 67.5) * mm, "end": v(-56.15, 48.18) * mm});
            skLineSegment(sketch, "E79.14", {"start": v(-60, 40.3) * mm, "end": v(-60, -40.3) * mm});
            skArc(sketch, "E79.15", {"start": v(-60, -40.3) * mm, "mid": v(-58.99, -44.68) * mm, "end": v(-56.15, -48.18) * mm});
            skArc(sketch, "E79.16", {"start": v(-56.15, -48.18) * mm, "mid": v(0, -67.5) * mm, "end": v(56.15, -48.18) * mm});
            skArc(sketch, "E79.17", {"start": v(56.15, -48.18) * mm, "mid": v(58.99, -44.68) * mm, "end": v(60, -40.3) * mm});
            skLineSegment(sketch, "E79.18", {"start": v(60, 40.3) * mm, "end": v(60, -40.3) * mm});
            skArc(sketch, "E79.19", {"start": v(60, 40.3) * mm, "mid": v(58.99, 44.68) * mm, "end": v(56.15, 48.18) * mm});
            skLineSegment(sketch, "E80", {"start": v(0, 90) * mm, "end": v(0, 120) * mm, "construction": true});
            skPoint(sketch, "E80.endSnap0", {"position": v(0, 90) * mm});
            skCircle(sketch, "E81", {"center": v(0, 120) * mm, "radius": 6 * mm});
            skArc(sketch, "E82", {"start": v(-15, 120) * mm, "mid": v(0, 135) * mm, "end": v(15, 120) * mm});
            skLineSegment(sketch, "E83", {"start": v(-33, 90) * mm, "end": v(-15, 108) * mm});
            skLineSegment(sketch, "E84", {"start": v(-15, 108) * mm, "end": v(-15, 120) * mm});
            skLineSegment(sketch, "E85", {"start": v(15, 120) * mm, "end": v(15, 108) * mm});
            skLineSegment(sketch, "E86", {"start": v(15, 108) * mm, "end": v(33, 90) * mm});
            skLineSegment(sketch, "E87", {"start": v(-80, 0) * mm, "end": v(80, 0) * mm, "construction": true});
            skLineSegment(sketch, "E88.MirrorCS", {"start": v(15, -120) * mm, "end": v(15, -108) * mm});
            skLineSegment(sketch, "E89.MirrorCS", {"start": v(-15, -108) * mm, "end": v(-15, -120) * mm});
            skCircle(sketch, "E90.MirrorC", {"center": v(0, -120) * mm, "radius": 6 * mm});
            skArc(sketch, "E91.MirrorCS", {"start": v(-15, -120) * mm, "mid": v(0, -135) * mm, "end": v(15, -120) * mm});
            skLineSegment(sketch, "E92.MirrorCS", {"start": v(-33, -90) * mm, "end": v(-15, -108) * mm});
            skLineSegment(sketch, "E93.MirrorCS", {"start": v(15, -108) * mm, "end": v(33, -90) * mm});
            skLineSegment(sketch, "E94.MirrorCS", {"start": v(0, -90) * mm, "end": v(0, -120) * mm, "construction": true});
            skSolve(sketch);
        }
        {
            var Q0;
            Q0=makeQuery(id+"F16.imprint","IMPRINT",FACE,{"disambiguationData":[TD([[makeQuery(id+"F16.imprint","IMPRINT",EDGE,{"derivedFrom":sQuery(id+"F16.wireOp",EDGE,"E81")}),-1.0]])]});
            var Q1;
            {var subQ1=sQuery(id+"F16.wireOp",EDGE,"E79.1");Q1=makeQuery(id+"F16.imprint","IMPRINT",FACE,{"disambiguationData":[TD([[makeQuery(id+"F16.imprint","IMPRINT",EDGE,{"derivedFrom":subQ1}),1.0]])]});}
            var Q2;
            Q2=makeQuery(id+"F16.imprint","IMPRINT",FACE,{"disambiguationData":[TD([[makeQuery(id+"F16.imprint","IMPRINT",EDGE,{"derivedFrom":sQuery(id+"F16.wireOp",EDGE,"E88.MirrorCS")}),1.0]])]});
            var Q3;
            Q3=makeQuery(id+"F2.opExtrude","CAP_FACE",FACE,{"disambiguationData":[OSD([sQuery(id+"F0.wireOp",EDGE,"E12"),sQuery(id+"F0.wireOp",EDGE,"E13"),sQuery(id+"F0.wireOp",EDGE,"E14"),sQuery(id+"F0.wireOp",EDGE,"E15"),sQuery(id+"F0.wireOp",EDGE,"E17.filletArc"),sQuery(id+"F0.wireOp",EDGE,"E18.filletArc"),sQuery(id+"F0.wireOp",EDGE,"E19.filletArc"),sQuery(id+"F0.wireOp",EDGE,"E20.filletArc"),sQuery(id+"F0.wireOp",EDGE,"E25.0"),sQuery(id+"F0.wireOp",EDGE,"E25.1"),sQuery(id+"F0.wireOp",EDGE,"E25.2"),sQuery(id+"F0.wireOp",EDGE,"E25.3"),sQuery(id+"F0.wireOp",EDGE,"E25.4"),sQuery(id+"F0.wireOp",EDGE,"E25.5"),sQuery(id+"F0.wireOp",EDGE,"E25.6"),sQuery(id+"F0.wireOp",EDGE,"E25.7")])],"isStart":false});
            extrude(context, id + "F17", {"entities" : qUnion([Q0, Q1, Q2]), "endBound" : BoundingType.UP_TO_SURFACE, "endBoundEntityFace" : qUnion([Q3]), "depth" : 25 * mm});
        }
    });
